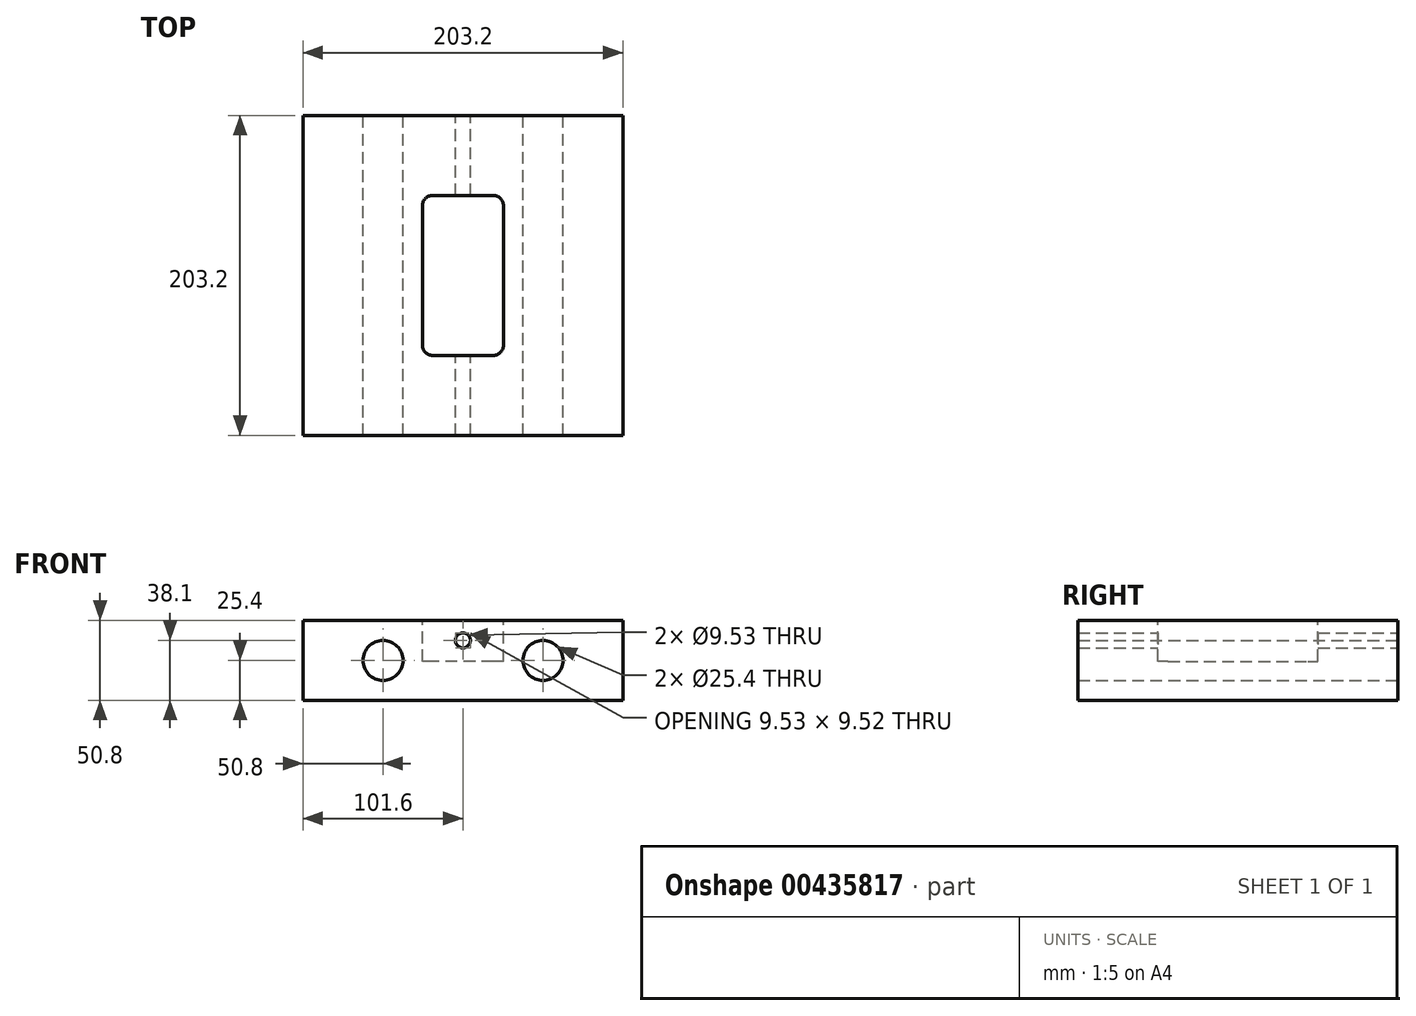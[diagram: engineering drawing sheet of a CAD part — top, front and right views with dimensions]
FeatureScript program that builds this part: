
annotation { "Feature Type Name" : "Feature", "Feature Type Description" : "" }
export const myFeature = defineFeature(function(context is Context, id is Id, definition is map)
    precondition{}
    {
        {
            var Q0;
            Q0=qCreatedBy(makeId("Front.planeOp"),FACE);
            var sketch = newSketch(context, id + "F0", { "sketchPlane" : qUnion([Q0])});
            skLineSegment(sketch, "E0.bottom", {"start": v(-101.6, -25.4) * mm, "end": v(101.6, -25.4) * mm});
            skLineSegment(sketch, "E0.top", {"start": v(-101.6, 25.4) * mm, "end": v(-26.03, 25.4) * mm});
            skLineSegment(sketch, "E0.left", {"start": v(-101.6, -25.4) * mm, "end": v(-101.6, 25.4) * mm});
            skLineSegment(sketch, "E0.right", {"start": v(101.6, -25.4) * mm, "end": v(101.6, 25.4) * mm});
            skPoint(sketch, "E0.middle", {"position": v(0, 0) * mm});
            skCircle(sketch, "E1", {"center": v(-50.8, 0) * mm, "radius": 12.7 * mm});
            skCircle(sketch, "E2", {"center": v(50.8, 0) * mm, "radius": 12.7 * mm});
            skCircle(sketch, "E3", {"center": v(0, 12.7) * mm, "radius": 4.76 * mm});
            skLineSegment(sketch, "E4.trimOffspring", {"start": v(26.04, 25.4) * mm, "end": v(101.6, 25.4) * mm});
            skLineSegment(sketch, "E5", {"start": v(-26.03, 25.4) * mm, "end": v(26.04, 25.4) * mm});
            skSolve(sketch);
        }
        {
            var Q0;
            Q0=makeQuery(id+"F0.imprint","IMPRINT",FACE,{"disambiguationData":[TD([[makeQuery(id+"F0.imprint","IMPRINT",EDGE,{"derivedFrom":sQuery(id+"F0.wireOp",EDGE,"E0.bottom")}),1.0]])]});
            extrude(context, id + "F1", {"entities" : qUnion([Q0]), "endBound" : BoundingType.SYMMETRIC, "depth" : 203.2 * mm});
        }
        {
            var Q0;
            Q0=makeQuery(id+"F1.opExtrude","SWEPT_FACE",FACE,{"disambiguationData":[OSD([sQuery(id+"F0.wireOp",EDGE,"E0.top"),sQuery(id+"F0.wireOp",EDGE,"E4.trimOffspring"),sQuery(id+"F0.wireOp",EDGE,"E5")])]});
            var sketch = newSketch(context, id + "F2", { "sketchPlane" : qUnion([Q0])});
            skLineSegment(sketch, "E6.bottom", {"start": v(19.37, -50.8) * mm, "end": v(-19.37, -50.8) * mm});
            skLineSegment(sketch, "E6.top", {"start": v(19.37, 50.8) * mm, "end": v(-19.37, 50.8) * mm});
            skLineSegment(sketch, "E6.left", {"start": v(25.72, -44.45) * mm, "end": v(25.72, 44.45) * mm});
            skLineSegment(sketch, "E6.right", {"start": v(-25.72, -44.45) * mm, "end": v(-25.72, 44.45) * mm});
            skPoint(sketch, "E6.middle", {"position": v(0, 0) * mm});
            skPoint(sketch, "E7.visualSharp", {"position": v(-25.72, 50.8) * mm});
            skArc(sketch, "E7.filletArc", {"start": v(-19.37, 50.8) * mm, "mid": v(-23.86, 48.94) * mm, "end": v(-25.72, 44.45) * mm});
            skPoint(sketch, "E8.visualSharp", {"position": v(25.72, 50.8) * mm});
            skArc(sketch, "E8.filletArc", {"start": v(25.72, 44.45) * mm, "mid": v(23.86, 48.94) * mm, "end": v(19.37, 50.8) * mm});
            skPoint(sketch, "E9.visualSharp", {"position": v(25.72, -50.8) * mm});
            skArc(sketch, "E9.filletArc", {"start": v(19.37, -50.8) * mm, "mid": v(23.86, -48.94) * mm, "end": v(25.72, -44.45) * mm});
            skPoint(sketch, "E10.visualSharp", {"position": v(-25.72, -50.8) * mm});
            skArc(sketch, "E10.filletArc", {"start": v(-25.72, -44.45) * mm, "mid": v(-23.86, -48.94) * mm, "end": v(-19.37, -50.8) * mm});
            skSolve(sketch);
        }
        {
            var Q0;
            Q0 = qSketchRegion(id + "F2", true);
            extrude(context, id + "F3", {"entities" : qUnion([Q0]), "operationType" : NewBodyOperationType.REMOVE, "oppositeDirection" : true, "depth" : 26.03 * mm});
        }
    });
